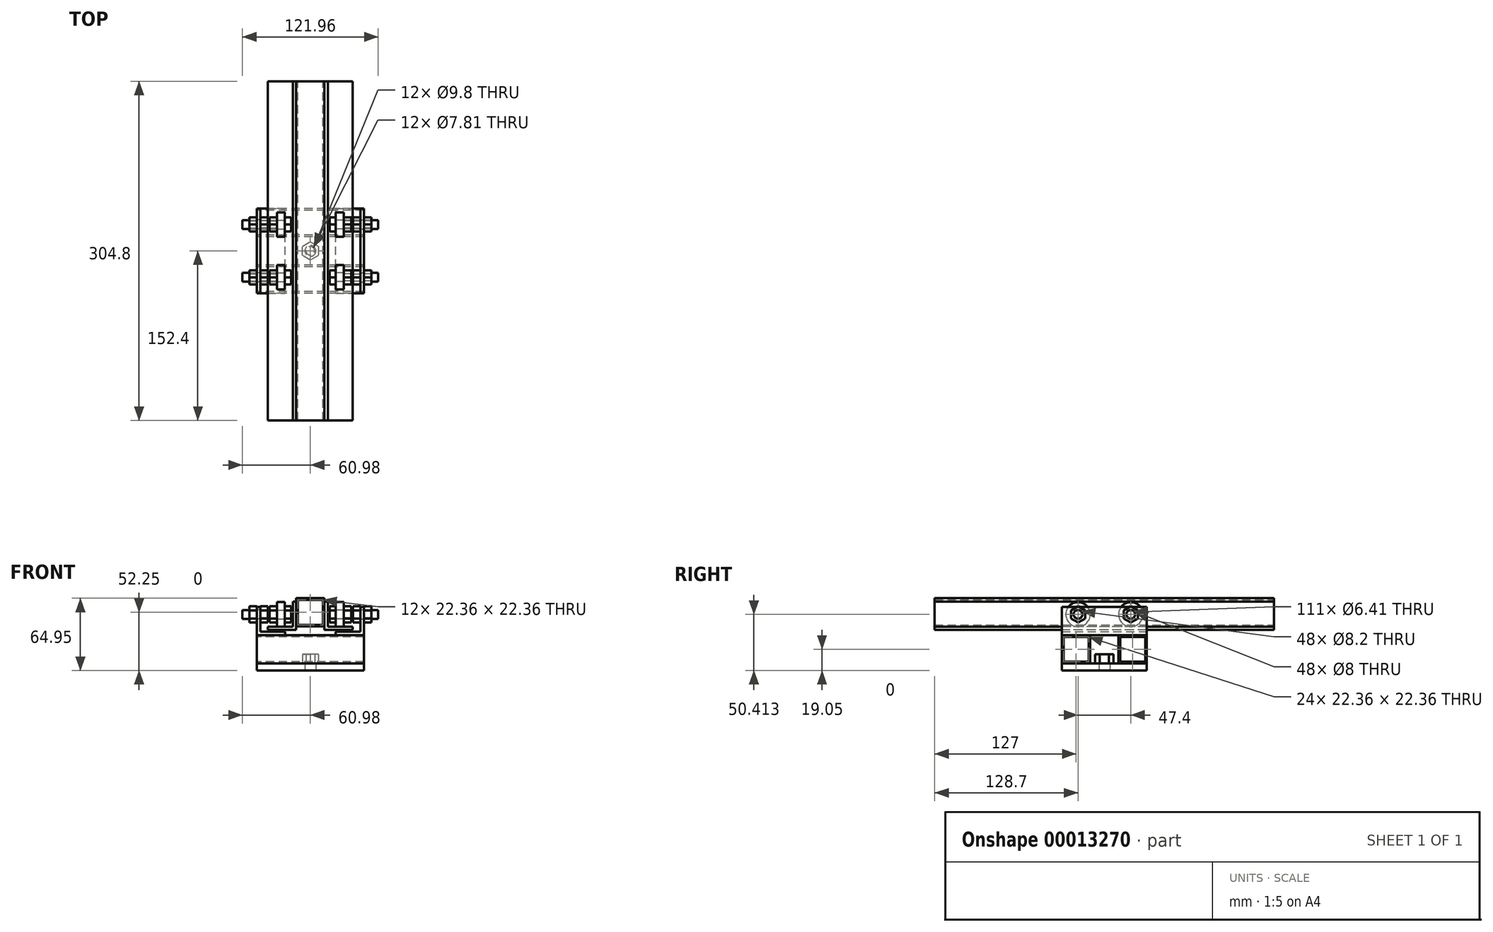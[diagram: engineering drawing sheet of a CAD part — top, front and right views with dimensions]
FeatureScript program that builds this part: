
annotation { "Feature Type Name" : "Feature", "Feature Type Description" : "" }
export const myFeature = defineFeature(function(context is Context, id is Id, definition is map)
    precondition{}
    {
        {
            var Q0;
            Q0=qCreatedBy(makeId("Front.planeOp"),FACE);
            var sketch = newSketch(context, id + "F0", { "sketchPlane" : qUnion([Q0])});
            skLineSegment(sketch, "E0.bottom", {"start": v(-12.7, 12.7) * mm, "end": v(12.7, 12.7) * mm});
            skLineSegment(sketch, "E0.top", {"start": v(-12.7, -12.7) * mm, "end": v(12.7, -12.7) * mm});
            skLineSegment(sketch, "E0.left", {"start": v(-12.7, 12.7) * mm, "end": v(-12.7, -12.7) * mm});
            skLineSegment(sketch, "E0.right", {"start": v(12.7, 12.7) * mm, "end": v(12.7, -12.7) * mm});
            skPoint(sketch, "E1", {"position": v(0, 12.7) * mm});
            skPoint(sketch, "E2", {"position": v(12.7, 0) * mm});
            skLineSegment(sketch, "E3.bottom", {"start": v(-11.18, 11.18) * mm, "end": v(11.18, 11.18) * mm});
            skLineSegment(sketch, "E3.top", {"start": v(-11.18, -11.18) * mm, "end": v(11.18, -11.18) * mm});
            skLineSegment(sketch, "E3.left", {"start": v(-11.18, 11.18) * mm, "end": v(-11.18, -11.18) * mm});
            skLineSegment(sketch, "E3.right", {"start": v(11.18, 11.18) * mm, "end": v(11.18, -11.18) * mm});
            skLineSegment(sketch, "E4", {"start": v(0, 12.7) * mm, "end": v(0, 11.18) * mm, "construction": true});
            skLineSegment(sketch, "E5", {"start": v(11.18, 0) * mm, "end": v(12.7, 0) * mm, "construction": true});
            skSolve(sketch);
        }
        {
            var Q0;
            Q0 = qSketchRegion(id + "F0", true);
            extrude(context, id + "F1", {"entities" : qUnion([Q0]), "depth" : 152.4 * mm, "hasSecondDirection" : true, "secondDirectionOppositeDirection" : true, "secondDirectionDepth" : 152.4 * mm});
        }
        {
            var Q0;
            Q0=makeQuery(id+"F1.opExtrude","CAP_FACE",FACE,{"disambiguationData":[OSD([sQuery(id+"F0.wireOp",EDGE,"E0.bottom"),sQuery(id+"F0.wireOp",EDGE,"E0.top"),sQuery(id+"F0.wireOp",EDGE,"E0.left"),sQuery(id+"F0.wireOp",EDGE,"E0.right"),sQuery(id+"F0.wireOp",EDGE,"E3.bottom"),sQuery(id+"F0.wireOp",EDGE,"E3.top"),sQuery(id+"F0.wireOp",EDGE,"E3.left"),sQuery(id+"F0.wireOp",EDGE,"E3.right")])],"isStart":false});
            var sketch = newSketch(context, id + "F2", { "sketchPlane" : qUnion([Q0])});
            skLineSegment(sketch, "E6", {"start": v(12.7, 9.52) * mm, "end": v(12.7, -15.88) * mm});
            skLineSegment(sketch, "E7", {"start": v(12.7, -15.88) * mm, "end": v(38.1, -15.88) * mm});
            skLineSegment(sketch, "E8", {"start": v(38.1, -15.88) * mm, "end": v(38.1, -12.84) * mm});
            skLineSegment(sketch, "E9", {"start": v(38.1, -12.84) * mm, "end": v(15.74, -12.84) * mm});
            skLineSegment(sketch, "E10", {"start": v(15.74, -12.84) * mm, "end": v(15.74, 9.52) * mm});
            skLineSegment(sketch, "E11", {"start": v(15.74, 9.52) * mm, "end": v(12.7, 9.52) * mm});
            skSolve(sketch);
        }
        {
            var Q0;
            Q0 = qSketchRegion(id + "F2", true);
            var Q1;
            Q1=makeQuery(id+"F1.opExtrude","CAP_FACE",FACE,{"disambiguationData":[OSD([sQuery(id+"F0.wireOp",EDGE,"E0.bottom"),sQuery(id+"F0.wireOp",EDGE,"E0.top"),sQuery(id+"F0.wireOp",EDGE,"E0.left"),sQuery(id+"F0.wireOp",EDGE,"E0.right"),sQuery(id+"F0.wireOp",EDGE,"E3.bottom"),sQuery(id+"F0.wireOp",EDGE,"E3.top"),sQuery(id+"F0.wireOp",EDGE,"E3.left"),sQuery(id+"F0.wireOp",EDGE,"E3.right")])],"isStart":true});
            extrude(context, id + "F3", {"entities" : qUnion([Q0]), "endBound" : BoundingType.UP_TO_SURFACE, "oppositeDirection" : true, "endBoundEntityFace" : qUnion([Q1]), "depth" : 25.4 * mm});
        }
        {
            var Q0;
            Q0=makeQuery(id+"F3.opExtrude","SWEPT_BODY",BODY,{"disambiguationData":[OSD([sQuery(id+"F2.wireOp",EDGE,"E6"),sQuery(id+"F2.wireOp",EDGE,"E7"),sQuery(id+"F2.wireOp",EDGE,"E8"),sQuery(id+"F2.wireOp",EDGE,"E9"),sQuery(id+"F2.wireOp",EDGE,"E10"),sQuery(id+"F2.wireOp",EDGE,"E11")])]});
            var Q1;
            Q1=qCreatedBy(makeId("Right.planeOp"),FACE);
            mirror(context, id + "F4", {"entities" : qUnion([Q0]), "mirrorPlane" : qUnion([Q1])});
        }
        {
            var Q0;
            Q0=makeQuery(id+"F3.opExtrude","SWEPT_FACE",FACE,{"disambiguationData":[OSD([sQuery(id+"F2.wireOp",EDGE,"E10")])]});
            cPlane(context, id + "F5", {"entities" : qUnion([Q0]), "cplaneType" : CPlaneType.OFFSET, "offset" : 7.14 * mm, "width" : 152.4 * mm, "height" : 152.4 * mm});
        }
        {
            var Q0;
            Q0=qCreatedBy(id+"F5.planeOp",FACE);
            var sketch = newSketch(context, id + "F6", { "sketchPlane" : qUnion([Q0])});
            skCircle(sketch, "E12", {"center": v(-23.7, -1.84) * mm, "radius": 11 * mm});
            skCircle(sketch, "E13", {"center": v(-23.7, -1.84) * mm, "radius": 4 * mm});
            skLineSegment(sketch, "E14", {"start": v(-12.7, 9.52) * mm, "end": v(-12.7, -12.84) * mm, "construction": true});
            skSolve(sketch);
        }
        {
            var Q0;
            Q0 = qSketchRegion(id + "F6", true);
            extrude(context, id + "F7", {"entities" : qUnion([Q0]), "depth" : 7 * mm});
        }
        {
            var Q0;
            Q0=makeQuery(id+"F7.opExtrude","SWEPT_BODY",BODY,{"disambiguationData":[OSD([sQuery(id+"F6.wireOp",EDGE,"E12"),sQuery(id+"F6.wireOp",EDGE,"E13")])]});
            var Q1;
            Q1=qCreatedBy(makeId("Front.planeOp"),FACE);
            mirror(context, id + "F8", {"entities" : qUnion([Q0]), "mirrorPlane" : qUnion([Q1])});
        }
        {
            var Q0;
            Q0=qCreatedBy(id+"F5.planeOp",FACE);
            var sketch = newSketch(context, id + "F9", { "sketchPlane" : qUnion([Q0])});
            skCircle(sketch, "E15.cCircle", {"center": v(-23.7, -1.84) * mm, "radius": 6.35 * mm, "construction": true});
            skLineSegment(sketch, "E15.0", {"start": v(-17.35, 1.83) * mm, "end": v(-17.35, -5.5) * mm});
            skLineSegment(sketch, "E15.1", {"start": v(-17.35, -5.5) * mm, "end": v(-23.7, -9.17) * mm});
            skLineSegment(sketch, "E15.2", {"start": v(-23.7, -9.17) * mm, "end": v(-30.05, -5.5) * mm});
            skLineSegment(sketch, "E15.3", {"start": v(-30.05, -5.5) * mm, "end": v(-30.05, 1.83) * mm});
            skLineSegment(sketch, "E15.4", {"start": v(-30.05, 1.83) * mm, "end": v(-23.7, 5.5) * mm});
            skLineSegment(sketch, "E15.5", {"start": v(-23.7, 5.5) * mm, "end": v(-17.35, 1.83) * mm});
            skPoint(sketch, "E15.0.midPoint", {"position": v(-17.35, -1.84) * mm});
            skSolve(sketch);
        }
        {
            var Q0;
            Q0 = qSketchRegion(id + "F9", true);
            extrude(context, id + "F10", {"entities" : qUnion([Q0]), "oppositeDirection" : true, "depth" : 5.56 * mm});
        }
        {
            var Q0;
            Q0=makeQuery(id+"F10.opExtrude","CAP_FACE",FACE,{"disambiguationData":[OSD([sQuery(id+"F9.wireOp",EDGE,"E15.0"),sQuery(id+"F9.wireOp",EDGE,"E15.1"),sQuery(id+"F9.wireOp",EDGE,"E15.2"),sQuery(id+"F9.wireOp",EDGE,"E15.3"),sQuery(id+"F9.wireOp",EDGE,"E15.4"),sQuery(id+"F9.wireOp",EDGE,"E15.5")])],"isStart":true});
            var sketch = newSketch(context, id + "F11", { "sketchPlane" : qUnion([Q0])});
            skCircle(sketch, "E16", {"center": v(-23.7, -1.84) * mm, "radius": 3.97 * mm});
            skSolve(sketch);
        }
        {
            var Q0;
            Q0=makeQuery(id+"F11.imprint","IMPRINT",FACE,{"disambiguationData":[TD([[makeQuery(id+"F11.imprint","IMPRINT",EDGE,{"derivedFrom":sQuery(id+"F11.wireOp",EDGE,"E16")}),1.0]])]});
            extrude(context, id + "F12", {"entities" : qUnion([Q0]), "operationType" : NewBodyOperationType.ADD, "depth" : 38.1 * mm});
        }
        {
            var Q0;
            Q0=makeQuery(id+"F7.opExtrude","CAP_FACE",FACE,{"disambiguationData":[OSD([sQuery(id+"F6.wireOp",EDGE,"E12"),sQuery(id+"F6.wireOp",EDGE,"E13")])],"isStart":false});
            var sketch = newSketch(context, id + "F13", { "sketchPlane" : qUnion([Q0])});
            skCircle(sketch, "E17.cCircle", {"center": v(-23.7, -1.84) * mm, "radius": 6.35 * mm, "construction": true});
            skLineSegment(sketch, "E17.0", {"start": v(-17.35, 1.83) * mm, "end": v(-17.35, -5.5) * mm});
            skLineSegment(sketch, "E17.1", {"start": v(-17.35, -5.5) * mm, "end": v(-23.7, -9.17) * mm});
            skLineSegment(sketch, "E17.2", {"start": v(-23.7, -9.17) * mm, "end": v(-30.05, -5.5) * mm});
            skLineSegment(sketch, "E17.3", {"start": v(-30.05, -5.5) * mm, "end": v(-30.05, 1.83) * mm});
            skLineSegment(sketch, "E17.4", {"start": v(-30.05, 1.83) * mm, "end": v(-23.7, 5.5) * mm});
            skLineSegment(sketch, "E17.5", {"start": v(-23.7, 5.5) * mm, "end": v(-17.35, 1.83) * mm});
            skPoint(sketch, "E17.0.midPoint", {"position": v(-17.35, -1.84) * mm});
            skCircle(sketch, "E18", {"center": v(-23.7, -1.84) * mm, "radius": 3.2 * mm});
            skSolve(sketch);
        }
        {
            var Q0;
            Q0 = qSketchRegion(id + "F13", true);
            extrude(context, id + "F14", {"entities" : qUnion([Q0]), "depth" : 6.75 * mm});
        }
        {
            var Q0;
            Q0=makeQuery(id+"F14.opExtrude","CAP_FACE",FACE,{"disambiguationData":[OSD([sQuery(id+"F13.wireOp",EDGE,"E17.0"),sQuery(id+"F13.wireOp",EDGE,"E17.1"),sQuery(id+"F13.wireOp",EDGE,"E17.2"),sQuery(id+"F13.wireOp",EDGE,"E17.3"),sQuery(id+"F13.wireOp",EDGE,"E17.4"),sQuery(id+"F13.wireOp",EDGE,"E17.5"),sQuery(id+"F13.wireOp",EDGE,"E18")])],"isStart":false});
            cPlane(context, id + "F15", {"entities" : qUnion([Q0]), "cplaneType" : CPlaneType.OFFSET, "offset" : 0.8 * mm, "width" : 152.4 * mm, "height" : 152.4 * mm});
        }
        {
            var Q0;
            Q0=makeQuery(id+"F14.opExtrude","SWEPT_BODY",BODY,{"disambiguationData":[OSD([sQuery(id+"F13.wireOp",EDGE,"E17.0"),sQuery(id+"F13.wireOp",EDGE,"E17.1"),sQuery(id+"F13.wireOp",EDGE,"E17.2"),sQuery(id+"F13.wireOp",EDGE,"E17.3"),sQuery(id+"F13.wireOp",EDGE,"E17.4"),sQuery(id+"F13.wireOp",EDGE,"E17.5"),sQuery(id+"F13.wireOp",EDGE,"E18")])]});
            var Q1;
            Q1=qCreatedBy(id+"F15.planeOp",FACE);
            mirror(context, id + "F16", {"entities" : qUnion([Q0]), "mirrorPlane" : qUnion([Q1])});
        }
        {
            var Q0;
            Q0=qCreatedBy(makeId("Front.planeOp"),FACE);
            var sketch = newSketch(context, id + "F17", { "sketchPlane" : qUnion([Q0])});
            skLineSegment(sketch, "E19", {"start": v(22.6, -17.46) * mm, "end": v(22.6, -20.5) * mm});
            skLineSegment(sketch, "E20", {"start": v(22.6, -20.5) * mm, "end": v(48, -20.5) * mm});
            skLineSegment(sketch, "E21", {"start": v(48, -20.5) * mm, "end": v(48, 4.9) * mm});
            skLineSegment(sketch, "E22", {"start": v(48, 4.9) * mm, "end": v(44.96, 4.9) * mm});
            skLineSegment(sketch, "E23", {"start": v(44.96, 4.9) * mm, "end": v(44.96, -17.46) * mm});
            skLineSegment(sketch, "E24", {"start": v(44.96, -17.46) * mm, "end": v(22.6, -17.46) * mm});
            skSolve(sketch);
        }
        {
            var Q0;
            Q0 = qSketchRegion(id + "F17", true);
            extrude(context, id + "F18", {"entities" : qUnion([Q0]), "depth" : 38.1 * mm, "hasSecondDirection" : true, "secondDirectionOppositeDirection" : true, "secondDirectionDepth" : 38.1 * mm});
        }
        {
            var Q0;
            Q0=makeQuery(id+"F18.opExtrude","CAP_EDGE",EDGE,{"disambiguationData":[OSD([sQuery(id+"F17.wireOp",EDGE,"E22")])],"isStart":false});
            cPlane(context, id + "F19", {"entities" : qUnion([Q0]), "cplaneType" : CPlaneType.MID_PLANE, "offset" : 152.4 * mm, "width" : 152.4 * mm, "height" : 152.4 * mm});
        }
        {
            var Q0;
            Q0=makeQuery(id+"F16.opPattern","COPY",BODY,{"derivedFrom":makeQuery(id+"F14.opExtrude","SWEPT_BODY",BODY,{"disambiguationData":[OSD([sQuery(id+"F13.wireOp",EDGE,"E17.0"),sQuery(id+"F13.wireOp",EDGE,"E17.1"),sQuery(id+"F13.wireOp",EDGE,"E17.2"),sQuery(id+"F13.wireOp",EDGE,"E17.3"),sQuery(id+"F13.wireOp",EDGE,"E17.4"),sQuery(id+"F13.wireOp",EDGE,"E17.5"),sQuery(id+"F13.wireOp",EDGE,"E18")])]}),"instanceName":"1"});
            var Q1;
            Q1=qCreatedBy(id+"F19.planeOp",FACE);
            mirror(context, id + "F20", {"entities" : qUnion([Q0]), "mirrorPlane" : qUnion([Q1])});
        }
        {
            var Q0;
            Q0=makeQuery(id+"F18.opExtrude","SWEPT_FACE",FACE,{"disambiguationData":[OSD([sQuery(id+"F17.wireOp",EDGE,"E21")])]});
            var sketch = newSketch(context, id + "F21", { "sketchPlane" : qUnion([Q0])});
            skCircle(sketch, "E25", {"center": v(23.7, -1.84) * mm, "radius": 4.1 * mm});
            skCircle(sketch, "E26.0.MirrorC", {"center": v(-23.7, -1.84) * mm, "radius": 4.1 * mm});
            skSolve(sketch);
        }
        {
            var Q0;
            Q0 = qSketchRegion(id + "F21", true);
            var Q1;
            Q1=makeQuery(id+"F18.opExtrude","SWEPT_FACE",FACE,{"disambiguationData":[OSD([sQuery(id+"F17.wireOp",EDGE,"E23")])]});
            extrude(context, id + "F22", {"entities" : qUnion([Q0]), "operationType" : NewBodyOperationType.REMOVE, "endBound" : BoundingType.UP_TO_SURFACE, "oppositeDirection" : true, "endBoundEntityFace" : qUnion([Q1]), "depth" : 25.4 * mm});
        }
        {
            var Q0;
            Q0=makeQuery(id+"F10.opExtrude","SWEPT_BODY",BODY,{"disambiguationData":[OSD([sQuery(id+"F9.wireOp",EDGE,"E15.0"),sQuery(id+"F9.wireOp",EDGE,"E15.1"),sQuery(id+"F9.wireOp",EDGE,"E15.2"),sQuery(id+"F9.wireOp",EDGE,"E15.3"),sQuery(id+"F9.wireOp",EDGE,"E15.4"),sQuery(id+"F9.wireOp",EDGE,"E15.5")])]});
            var Q1;
            Q1=makeQuery(id+"F14.opExtrude","SWEPT_BODY",BODY,{"disambiguationData":[OSD([sQuery(id+"F13.wireOp",EDGE,"E17.0"),sQuery(id+"F13.wireOp",EDGE,"E17.1"),sQuery(id+"F13.wireOp",EDGE,"E17.2"),sQuery(id+"F13.wireOp",EDGE,"E17.3"),sQuery(id+"F13.wireOp",EDGE,"E17.4"),sQuery(id+"F13.wireOp",EDGE,"E17.5"),sQuery(id+"F13.wireOp",EDGE,"E18")])]});
            var Q2;
            Q2=makeQuery(id+"F16.opPattern","COPY",BODY,{"derivedFrom":makeQuery(id+"F14.opExtrude","SWEPT_BODY",BODY,{"disambiguationData":[OSD([sQuery(id+"F13.wireOp",EDGE,"E17.0"),sQuery(id+"F13.wireOp",EDGE,"E17.1"),sQuery(id+"F13.wireOp",EDGE,"E17.2"),sQuery(id+"F13.wireOp",EDGE,"E17.3"),sQuery(id+"F13.wireOp",EDGE,"E17.4"),sQuery(id+"F13.wireOp",EDGE,"E17.5"),sQuery(id+"F13.wireOp",EDGE,"E18")])]}),"instanceName":"1"});
            var Q3;
            Q3=makeQuery(id+"F20.opPattern","COPY",BODY,{"derivedFrom":makeQuery(id+"F16.opPattern","COPY",BODY,{"derivedFrom":makeQuery(id+"F14.opExtrude","SWEPT_BODY",BODY,{"disambiguationData":[OSD([sQuery(id+"F13.wireOp",EDGE,"E17.0"),sQuery(id+"F13.wireOp",EDGE,"E17.1"),sQuery(id+"F13.wireOp",EDGE,"E17.2"),sQuery(id+"F13.wireOp",EDGE,"E17.3"),sQuery(id+"F13.wireOp",EDGE,"E17.4"),sQuery(id+"F13.wireOp",EDGE,"E17.5"),sQuery(id+"F13.wireOp",EDGE,"E18")])]}),"instanceName":"1"}),"instanceName":"1"});
            var Q4;
            Q4=qCreatedBy(makeId("Front.planeOp"),FACE);
            mirror(context, id + "F23", {"entities" : qUnion([Q0, Q1, Q2, Q3]), "mirrorPlane" : qUnion([Q4])});
        }
        {
            var Q0;
            Q0=makeQuery(id+"F10.opExtrude","SWEPT_BODY",BODY,{"disambiguationData":[OSD([sQuery(id+"F9.wireOp",EDGE,"E15.0"),sQuery(id+"F9.wireOp",EDGE,"E15.1"),sQuery(id+"F9.wireOp",EDGE,"E15.2"),sQuery(id+"F9.wireOp",EDGE,"E15.3"),sQuery(id+"F9.wireOp",EDGE,"E15.4"),sQuery(id+"F9.wireOp",EDGE,"E15.5")])]});
            var Q1;
            Q1=makeQuery(id+"F7.opExtrude","SWEPT_BODY",BODY,{"disambiguationData":[OSD([sQuery(id+"F6.wireOp",EDGE,"E12"),sQuery(id+"F6.wireOp",EDGE,"E13")])]});
            var Q2;
            Q2=makeQuery(id+"F14.opExtrude","SWEPT_BODY",BODY,{"disambiguationData":[OSD([sQuery(id+"F13.wireOp",EDGE,"E17.0"),sQuery(id+"F13.wireOp",EDGE,"E17.1"),sQuery(id+"F13.wireOp",EDGE,"E17.2"),sQuery(id+"F13.wireOp",EDGE,"E17.3"),sQuery(id+"F13.wireOp",EDGE,"E17.4"),sQuery(id+"F13.wireOp",EDGE,"E17.5"),sQuery(id+"F13.wireOp",EDGE,"E18")])]});
            var Q3;
            Q3=makeQuery(id+"F16.opPattern","COPY",BODY,{"derivedFrom":makeQuery(id+"F14.opExtrude","SWEPT_BODY",BODY,{"disambiguationData":[OSD([sQuery(id+"F13.wireOp",EDGE,"E17.0"),sQuery(id+"F13.wireOp",EDGE,"E17.1"),sQuery(id+"F13.wireOp",EDGE,"E17.2"),sQuery(id+"F13.wireOp",EDGE,"E17.3"),sQuery(id+"F13.wireOp",EDGE,"E17.4"),sQuery(id+"F13.wireOp",EDGE,"E17.5"),sQuery(id+"F13.wireOp",EDGE,"E18")])]}),"instanceName":"1"});
            var Q4;
            Q4=makeQuery(id+"F20.opPattern","COPY",BODY,{"derivedFrom":makeQuery(id+"F16.opPattern","COPY",BODY,{"derivedFrom":makeQuery(id+"F14.opExtrude","SWEPT_BODY",BODY,{"disambiguationData":[OSD([sQuery(id+"F13.wireOp",EDGE,"E17.0"),sQuery(id+"F13.wireOp",EDGE,"E17.1"),sQuery(id+"F13.wireOp",EDGE,"E17.2"),sQuery(id+"F13.wireOp",EDGE,"E17.3"),sQuery(id+"F13.wireOp",EDGE,"E17.4"),sQuery(id+"F13.wireOp",EDGE,"E17.5"),sQuery(id+"F13.wireOp",EDGE,"E18")])]}),"instanceName":"1"}),"instanceName":"1"});
            var Q5;
            Q5=makeQuery(id+"F23.opPattern","COPY",BODY,{"derivedFrom":makeQuery(id+"F10.opExtrude","SWEPT_BODY",BODY,{"disambiguationData":[OSD([sQuery(id+"F9.wireOp",EDGE,"E15.0"),sQuery(id+"F9.wireOp",EDGE,"E15.1"),sQuery(id+"F9.wireOp",EDGE,"E15.2"),sQuery(id+"F9.wireOp",EDGE,"E15.3"),sQuery(id+"F9.wireOp",EDGE,"E15.4"),sQuery(id+"F9.wireOp",EDGE,"E15.5")])]}),"instanceName":"1"});
            var Q6;
            Q6=makeQuery(id+"F8.opPattern","COPY",BODY,{"derivedFrom":makeQuery(id+"F7.opExtrude","SWEPT_BODY",BODY,{"disambiguationData":[OSD([sQuery(id+"F6.wireOp",EDGE,"E12"),sQuery(id+"F6.wireOp",EDGE,"E13")])]}),"instanceName":"1"});
            var Q7;
            Q7=makeQuery(id+"F23.opPattern","COPY",BODY,{"derivedFrom":makeQuery(id+"F14.opExtrude","SWEPT_BODY",BODY,{"disambiguationData":[OSD([sQuery(id+"F13.wireOp",EDGE,"E17.0"),sQuery(id+"F13.wireOp",EDGE,"E17.1"),sQuery(id+"F13.wireOp",EDGE,"E17.2"),sQuery(id+"F13.wireOp",EDGE,"E17.3"),sQuery(id+"F13.wireOp",EDGE,"E17.4"),sQuery(id+"F13.wireOp",EDGE,"E17.5"),sQuery(id+"F13.wireOp",EDGE,"E18")])]}),"instanceName":"1"});
            var Q8;
            Q8=makeQuery(id+"F23.opPattern","COPY",BODY,{"derivedFrom":makeQuery(id+"F16.opPattern","COPY",BODY,{"derivedFrom":makeQuery(id+"F14.opExtrude","SWEPT_BODY",BODY,{"disambiguationData":[OSD([sQuery(id+"F13.wireOp",EDGE,"E17.0"),sQuery(id+"F13.wireOp",EDGE,"E17.1"),sQuery(id+"F13.wireOp",EDGE,"E17.2"),sQuery(id+"F13.wireOp",EDGE,"E17.3"),sQuery(id+"F13.wireOp",EDGE,"E17.4"),sQuery(id+"F13.wireOp",EDGE,"E17.5"),sQuery(id+"F13.wireOp",EDGE,"E18")])]}),"instanceName":"1"}),"instanceName":"1"});
            var Q9;
            Q9=makeQuery(id+"F23.opPattern","COPY",BODY,{"derivedFrom":makeQuery(id+"F20.opPattern","COPY",BODY,{"derivedFrom":makeQuery(id+"F16.opPattern","COPY",BODY,{"derivedFrom":makeQuery(id+"F14.opExtrude","SWEPT_BODY",BODY,{"disambiguationData":[OSD([sQuery(id+"F13.wireOp",EDGE,"E17.0"),sQuery(id+"F13.wireOp",EDGE,"E17.1"),sQuery(id+"F13.wireOp",EDGE,"E17.2"),sQuery(id+"F13.wireOp",EDGE,"E17.3"),sQuery(id+"F13.wireOp",EDGE,"E17.4"),sQuery(id+"F13.wireOp",EDGE,"E17.5"),sQuery(id+"F13.wireOp",EDGE,"E18")])]}),"instanceName":"1"}),"instanceName":"1"}),"instanceName":"1"});
            var Q10;
            Q10=makeQuery(id+"F18.opExtrude","SWEPT_BODY",BODY,{"disambiguationData":[OSD([sQuery(id+"F17.wireOp",EDGE,"E19"),sQuery(id+"F17.wireOp",EDGE,"E20"),sQuery(id+"F17.wireOp",EDGE,"E21"),sQuery(id+"F17.wireOp",EDGE,"E22"),sQuery(id+"F17.wireOp",EDGE,"E23"),sQuery(id+"F17.wireOp",EDGE,"E24")])]});
            var Q11;
            Q11=qCreatedBy(makeId("Right.planeOp"),FACE);
            mirror(context, id + "F24", {"entities" : qUnion([Q0, Q1, Q2, Q3, Q4, Q5, Q6, Q7, Q8, Q9, Q10]), "mirrorPlane" : qUnion([Q11])});
        }
        {
            var Q0;
            Q0=makeQuery(id+"F24.opPattern","COPY",FACE,{"derivedFrom":makeQuery(id+"F18.opExtrude","SWEPT_FACE",FACE,{"disambiguationData":[OSD([sQuery(id+"F17.wireOp",EDGE,"E21")])]}),"instanceName":"1"});
            var sketch = newSketch(context, id + "F25", { "sketchPlane" : qUnion([Q0])});
            skLineSegment(sketch, "E27.bottom", {"start": v(38.1, -20.5) * mm, "end": v(12.7, -20.5) * mm});
            skLineSegment(sketch, "E27.top", {"start": v(38.1, -45.9) * mm, "end": v(12.7, -45.9) * mm});
            skLineSegment(sketch, "E27.left", {"start": v(38.1, -20.5) * mm, "end": v(38.1, -45.9) * mm});
            skLineSegment(sketch, "E27.right", {"start": v(12.7, -20.5) * mm, "end": v(12.7, -45.9) * mm});
            skLineSegment(sketch, "E28.bottom", {"start": v(36.58, -22.02) * mm, "end": v(14.22, -22.02) * mm});
            skLineSegment(sketch, "E28.top", {"start": v(36.58, -44.38) * mm, "end": v(14.22, -44.38) * mm});
            skLineSegment(sketch, "E28.left", {"start": v(36.58, -22.02) * mm, "end": v(36.58, -44.38) * mm});
            skLineSegment(sketch, "E28.right", {"start": v(14.22, -22.02) * mm, "end": v(14.22, -44.38) * mm});
            skLineSegment(sketch, "E29", {"start": v(36.58, -33.2) * mm, "end": v(38.1, -33.2) * mm, "construction": true});
            skLineSegment(sketch, "E30", {"start": v(25.4, -44.38) * mm, "end": v(25.4, -45.9) * mm, "construction": true});
            skSolve(sketch);
        }
        {
            var Q0;
            Q0 = qSketchRegion(id + "F25", true);
            var Q1;
            Q1=makeQuery(id+"F18.opExtrude","SWEPT_FACE",FACE,{"disambiguationData":[OSD([sQuery(id+"F17.wireOp",EDGE,"E21")])]});
            extrude(context, id + "F26", {"entities" : qUnion([Q0]), "endBound" : BoundingType.UP_TO_SURFACE, "oppositeDirection" : true, "endBoundEntityFace" : qUnion([Q1]), "depth" : 25.4 * mm});
        }
        {
            var Q0;
            Q0=makeQuery(id+"F26.opExtrude","SWEPT_BODY",BODY,{"disambiguationData":[OSD([sQuery(id+"F25.wireOp",EDGE,"E27.bottom"),sQuery(id+"F25.wireOp",EDGE,"E27.top"),sQuery(id+"F25.wireOp",EDGE,"E27.left"),sQuery(id+"F25.wireOp",EDGE,"E27.right"),sQuery(id+"F25.wireOp",EDGE,"E28.bottom"),sQuery(id+"F25.wireOp",EDGE,"E28.top"),sQuery(id+"F25.wireOp",EDGE,"E28.left"),sQuery(id+"F25.wireOp",EDGE,"E28.right")])]});
            var Q1;
            Q1=qCreatedBy(makeId("Front.planeOp"),FACE);
            mirror(context, id + "F27", {"entities" : qUnion([Q0]), "mirrorPlane" : qUnion([Q1])});
        }
        {
            var Q0;
            Q0=makeQuery(id+"F27.opPattern","COPY",FACE,{"derivedFrom":makeQuery(id+"F26.opExtrude","SWEPT_FACE",FACE,{"disambiguationData":[OSD([sQuery(id+"F25.wireOp",EDGE,"E27.top")])]}),"instanceName":"1"});
            var sketch = newSketch(context, id + "F28", { "sketchPlane" : qUnion([Q0])});
            skLineSegment(sketch, "E31.bottom", {"start": v(-48, -38.1) * mm, "end": v(48, -38.1) * mm});
            skLineSegment(sketch, "E31.top", {"start": v(-48, 38.1) * mm, "end": v(48, 38.1) * mm});
            skLineSegment(sketch, "E31.left", {"start": v(-48, -38.1) * mm, "end": v(-48, 38.1) * mm});
            skLineSegment(sketch, "E31.right", {"start": v(48, -38.1) * mm, "end": v(48, 38.1) * mm});
            skSolve(sketch);
        }
        {
            var Q0;
            Q0 = qSketchRegion(id + "F28", true);
            extrude(context, id + "F29", {"entities" : qUnion([Q0]), "depth" : 6.35 * mm});
        }
        {
            var Q0;
            Q0=makeQuery(id+"F29.opExtrude","CAP_FACE",FACE,{"disambiguationData":[OSD([sQuery(id+"F28.wireOp",EDGE,"E31.bottom"),sQuery(id+"F28.wireOp",EDGE,"E31.top"),sQuery(id+"F28.wireOp",EDGE,"E31.left"),sQuery(id+"F28.wireOp",EDGE,"E31.right")])],"isStart":false});
            var sketch = newSketch(context, id + "F30", { "sketchPlane" : qUnion([Q0])});
            skCircle(sketch, "E32", {"center": v(0, 0) * mm, "radius": 4.9 * mm});
            skSolve(sketch);
        }
        {
            var Q0;
            Q0 = qSketchRegion(id + "F30", true);
            var Q1;
            Q1=makeQuery(id+"F29.opExtrude","CAP_FACE",FACE,{"disambiguationData":[OSD([sQuery(id+"F28.wireOp",EDGE,"E31.bottom"),sQuery(id+"F28.wireOp",EDGE,"E31.top"),sQuery(id+"F28.wireOp",EDGE,"E31.left"),sQuery(id+"F28.wireOp",EDGE,"E31.right")])],"isStart":true});
            extrude(context, id + "F31", {"entities" : qUnion([Q0]), "operationType" : NewBodyOperationType.REMOVE, "endBound" : BoundingType.UP_TO_SURFACE, "oppositeDirection" : true, "endBoundEntityFace" : qUnion([Q1]), "depth" : 25.4 * mm});
        }
        {
            var Q0;
            Q0=makeQuery(id+"F29.opExtrude","CAP_FACE",FACE,{"disambiguationData":[OSD([sQuery(id+"F28.wireOp",EDGE,"E31.bottom"),sQuery(id+"F28.wireOp",EDGE,"E31.top"),sQuery(id+"F28.wireOp",EDGE,"E31.left"),sQuery(id+"F28.wireOp",EDGE,"E31.right")])],"isStart":true});
            var sketch = newSketch(context, id + "F32", { "sketchPlane" : qUnion([Q0])});
            skCircle(sketch, "E33.cCircle", {"center": v(0, 0) * mm, "radius": 7.14 * mm, "construction": true});
            skLineSegment(sketch, "E33.0", {"start": v(-7.14, -4.12) * mm, "end": v(-7.14, 4.12) * mm});
            skLineSegment(sketch, "E33.1", {"start": v(-7.14, 4.12) * mm, "end": v(0, 8.25) * mm});
            skLineSegment(sketch, "E33.2", {"start": v(0, 8.25) * mm, "end": v(7.14, 4.12) * mm});
            skLineSegment(sketch, "E33.3", {"start": v(7.14, 4.12) * mm, "end": v(7.14, -4.12) * mm});
            skLineSegment(sketch, "E33.4", {"start": v(7.14, -4.12) * mm, "end": v(0, -8.25) * mm});
            skLineSegment(sketch, "E33.5", {"start": v(0, -8.25) * mm, "end": v(-7.14, -4.12) * mm});
            skPoint(sketch, "E33.0.midPoint", {"position": v(-7.14, 0) * mm});
            skCircle(sketch, "E34", {"center": v(0, 0) * mm, "radius": 3.9 * mm});
            skSolve(sketch);
        }
        {
            var Q0;
            Q0 = qSketchRegion(id + "F32", true);
            extrude(context, id + "F33", {"entities" : qUnion([Q0]), "depth" : 8.33 * mm});
        }
    });
